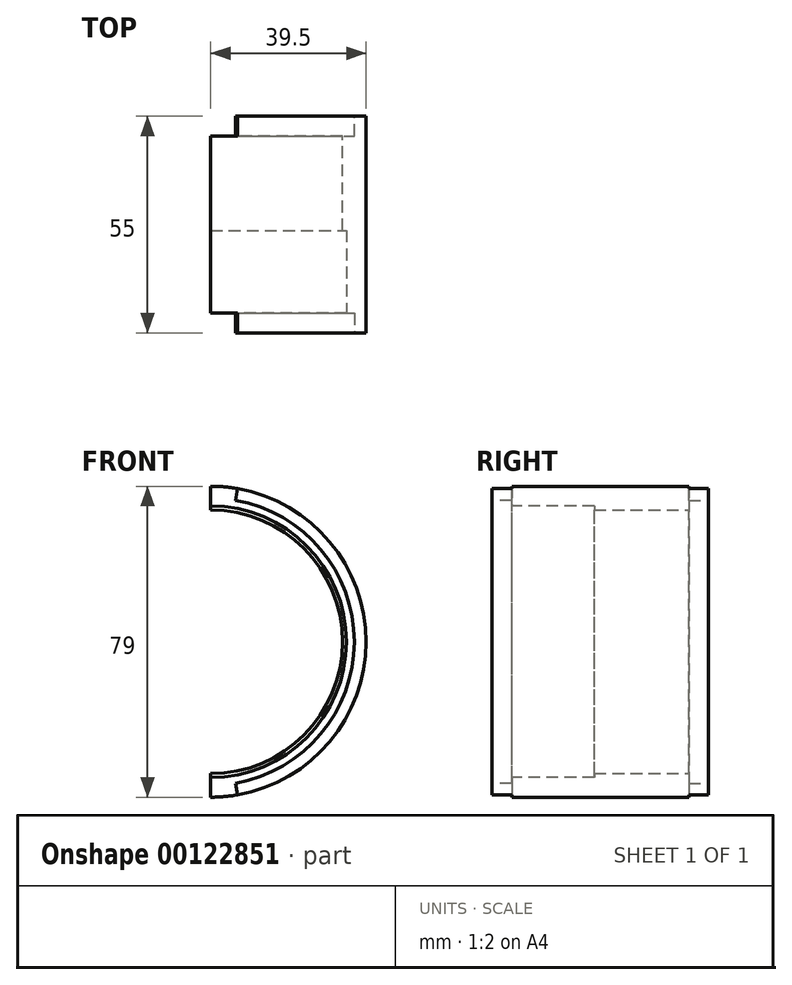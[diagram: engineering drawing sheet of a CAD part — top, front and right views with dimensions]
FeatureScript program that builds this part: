
annotation { "Feature Type Name" : "Feature", "Feature Type Description" : "" }
export const myFeature = defineFeature(function(context is Context, id is Id, definition is map)
    precondition{}
    {
        {
            var Q0;
            Q0=qCreatedBy(makeId("Front.planeOp"),FACE);
            var sketch = newSketch(context, id + "F0", { "sketchPlane" : qUnion([Q0])});
            skArc(sketch, "E0", {"start": v(0, -39.5) * mm, "mid": v(39.5, 0) * mm, "end": v(0, 39.5) * mm});
            skArc(sketch, "E1", {"start": v(0, -33.5) * mm, "mid": v(33.5, 0) * mm, "end": v(0, 33.5) * mm});
            skLineSegment(sketch, "E2", {"start": v(0, 39.5) * mm, "end": v(0, 33.5) * mm});
            skLineSegment(sketch, "E3.trimOffspring", {"start": v(0, -33.5) * mm, "end": v(0, -39.5) * mm});
            skLineSegment(sketch, "E4", {"start": v(0, 0) * mm, "end": v(15.65, 53.42) * mm, "construction": true});
            skSolve(sketch);
        }
        {
            var Q0;
            Q0 = qSketchRegion(id + "F0", true);
            extrude(context, id + "F1", {"entities" : qUnion([Q0]), "depth" : 55 * mm});
        }
        {
            var Q0;
            Q0=makeQuery(id+"F1.opExtrude","CAP_FACE",FACE,{"disambiguationData":[OSD([sQuery(id+"F0.wireOp",EDGE,"E0"),sQuery(id+"F0.wireOp",EDGE,"E1"),sQuery(id+"F0.wireOp",EDGE,"E2"),sQuery(id+"F0.wireOp",EDGE,"E3.trimOffspring")])],"isStart":false});
            var sketch = newSketch(context, id + "F2", { "sketchPlane" : qUnion([Q0])});
            skArc(sketch, "E5", {"start": v(6.34, -35.95) * mm, "mid": v(36.5, 0) * mm, "end": v(6.34, 35.95) * mm});
            skArc(sketch, "E6", {"start": v(0, -33.5) * mm, "mid": v(33.5, 0) * mm, "end": v(0, 33.5) * mm});
            skArc(sketch, "E7", {"start": v(0, -39.5) * mm, "mid": v(3.44, -39.35) * mm, "end": v(6.86, -38.9) * mm});
            skLineSegment(sketch, "E8", {"start": v(0, 0) * mm, "end": v(5.82, -33) * mm, "construction": true});
            skLineSegment(sketch, "E9", {"start": v(0, 0) * mm, "end": v(5.82, 33) * mm, "construction": true});
            skLineSegment(sketch, "E10", {"start": v(0, 39.5) * mm, "end": v(0, 33.5) * mm});
            skLineSegment(sketch, "E11.trimOffspring", {"start": v(6.34, 35.95) * mm, "end": v(6.86, 38.9) * mm});
            skLineSegment(sketch, "E12.trimOffspring", {"start": v(6.34, -35.95) * mm, "end": v(6.86, -38.9) * mm});
            skLineSegment(sketch, "E13", {"start": v(0, -39.5) * mm, "end": v(0, -33.5) * mm});
            skArc(sketch, "E14.trimOffspring", {"start": v(6.86, 38.9) * mm, "mid": v(3.44, 39.35) * mm, "end": v(0, 39.5) * mm});
            skSolve(sketch);
        }
        {
            var Q0;
            Q0 = qSketchRegion(id + "F2", true);
            extrude(context, id + "F3", {"entities" : qUnion([Q0]), "operationType" : NewBodyOperationType.REMOVE, "oppositeDirection" : true, "depth" : 5 * mm});
        }
        {
            var Q0;
            Q0=makeQuery(id+"F1.opExtrude","CAP_FACE",FACE,{"disambiguationData":[OSD([sQuery(id+"F0.wireOp",EDGE,"E0"),sQuery(id+"F0.wireOp",EDGE,"E1"),sQuery(id+"F0.wireOp",EDGE,"E2"),sQuery(id+"F0.wireOp",EDGE,"E3.trimOffspring")])],"isStart":true});
            var sketch = newSketch(context, id + "F4", { "sketchPlane" : qUnion([Q0])});
            skArc(sketch, "E15", {"start": v(-6.34, 35.95) * mm, "mid": v(-36.5, 0) * mm, "end": v(-6.34, -35.95) * mm});
            skArc(sketch, "E16", {"start": v(0, 33.5) * mm, "mid": v(-33.5, 0) * mm, "end": v(0, -33.5) * mm});
            skLineSegment(sketch, "E17", {"start": v(0, 39.5) * mm, "end": v(0, 33.5) * mm});
            skLineSegment(sketch, "E18.trimOffspring", {"start": v(0, -33.5) * mm, "end": v(0, -39.5) * mm});
            skArc(sketch, "E19", {"start": v(-6.86, -38.9) * mm, "mid": v(-3.44, -39.35) * mm, "end": v(0, -39.5) * mm});
            skLineSegment(sketch, "E20", {"start": v(0, 0) * mm, "end": v(-5.82, 33) * mm, "construction": true});
            skLineSegment(sketch, "E21", {"start": v(0, 0) * mm, "end": v(-5.82, -33) * mm, "construction": true});
            skLineSegment(sketch, "E22.trimOffspring", {"start": v(-6.34, 35.95) * mm, "end": v(-6.86, 38.9) * mm});
            skLineSegment(sketch, "E23.trimOffspring", {"start": v(-6.34, -35.95) * mm, "end": v(-6.86, -38.9) * mm});
            skArc(sketch, "E24.trimOffspring", {"start": v(0, 39.5) * mm, "mid": v(-3.44, 39.35) * mm, "end": v(-6.86, 38.9) * mm});
            skSolve(sketch);
        }
        {
            var Q0;
            Q0 = qSketchRegion(id + "F4", true);
            extrude(context, id + "F5", {"entities" : qUnion([Q0]), "operationType" : NewBodyOperationType.REMOVE, "oppositeDirection" : true, "depth" : 5 * mm});
        }
        {
            var Q0;
            Q0=makeQuery(id+"F1.opExtrude","CAP_FACE",FACE,{"disambiguationData":[OSD([sQuery(id+"F0.wireOp",EDGE,"E0"),sQuery(id+"F0.wireOp",EDGE,"E1"),sQuery(id+"F0.wireOp",EDGE,"E2"),sQuery(id+"F0.wireOp",EDGE,"E3.trimOffspring")])],"isStart":false});
            var sketch = newSketch(context, id + "F6", { "sketchPlane" : qUnion([Q0])});
            skCircle(sketch, "E25", {"center": v(0, 0) * mm, "radius": 34.5 * mm});
            skCircle(sketch, "E26", {"center": v(0, 0) * mm, "radius": 33.5 * mm});
            skSolve(sketch);
        }
        {
            var Q0;
            Q0 = qSketchRegion(id + "F6", true);
            extrude(context, id + "F7", {"entities" : qUnion([Q0]), "operationType" : NewBodyOperationType.REMOVE, "oppositeDirection" : true, "depth" : 26 * mm});
        }
    });
